FCSTD DOCUMENT  (FreeCAD 0.19R)
Label: card
License: All rights reserved
LicenseURL: http://en.wikipedia.org/wiki/All_rights_reserved
objects: Sketcher::SketchObject×1, PartDesign::Body×1
note: 2 computed .brp shape members not serialized (recipe doc carries the construction recipe); baked Part::Feature solids carry a one-line shape summary decoded from their .brp

FEATURE [Sketcher::SketchObject] Sketch
  FullyConstrained = true
  MapMode = 5
  Support = -> [XY_Plane]
  sketch-geometry (15):
    g0: LineSegment StartX=-48 StartY=35.5 StartZ=0 EndX=48 EndY=35.5 EndZ=0
    g1: LineSegment StartX=50 StartY=33.5 StartZ=0 EndX=50 EndY=-33.5 EndZ=0
    g2: LineSegment StartX=48 StartY=-35.5 StartZ=0 EndX=-48 EndY=-35.5 EndZ=0
    g3: LineSegment StartX=-50 StartY=-33.5 StartZ=0 EndX=-50 EndY=33.5 EndZ=0
    g4: LineSegment StartX=-50 StartY=35.5 StartZ=0 EndX=50 EndY=-35.5 EndZ=0
    g5: LineSegment StartX=50 StartY=35.5 StartZ=0 EndX=-50 EndY=-35.5 EndZ=0
    g6: GeomPoint X=0 Y=0 Z=0
    g7: ArcOfCircle CenterX=-48 CenterY=33.5 CenterZ=0 NormalX=0 NormalY=0 NormalZ=1 AngleXU=0 Radius=2 StartAngle=1.5708 EndAngle=3.14159
    g8: GeomPoint X=-50 Y=35.5 Z=0
    g9: ArcOfCircle CenterX=48 CenterY=33.5 CenterZ=0 NormalX=0 NormalY=0 NormalZ=1 AngleXU=0 Radius=2 StartAngle=1e-16 EndAngle=1.5708
    g10: GeomPoint X=50 Y=35.5 Z=0
    g11: ArcOfCircle CenterX=48 CenterY=-33.5 CenterZ=0 NormalX=0 NormalY=0 NormalZ=1 AngleXU=0 Radius=2 StartAngle=4.71239 EndAngle=6.28319
    g12: GeomPoint X=50 Y=-35.5 Z=0
    g13: ArcOfCircle CenterX=-48 CenterY=-33.5 CenterZ=0 NormalX=0 NormalY=0 NormalZ=1 AngleXU=0 Radius=2 StartAngle=3.14159 EndAngle=4.71239
    g14: GeomPoint X=-50 Y=-35.5 Z=0
  constraints (33):
    c: Horizontal(g0)
    c: Horizontal(g2)
    c: Vertical(g1)
    c: Vertical(g3)
    c: Coincident(g4,g8)
    c: Coincident(g4,g12)
    c: Coincident(g5,g10)
    c: Coincident(g5,g14)
    c: PointOnObject(g6,g4)
    c: PointOnObject(g6,g5)
    c: Coincident(g6,g-1)
    c: DistanceX(g8,g10) = 100
    c: DistanceY(g12,g10) = 71
    c: PointOnObject(g8,g0)
    c: PointOnObject(g8,g3)
    c: Tangent(g0,g7) = 1.5708
    c: Tangent(g3,g7) = 1.5708
    c: Radius(g7) = 2
    c: PointOnObject(g10,g1)
    c: PointOnObject(g10,g0)
    c: Tangent(g1,g9) = 1.5708
    c: Tangent(g0,g9) = 1.5708
    c: Radius(g9) = 2
    c: PointOnObject(g12,g1)
    c: PointOnObject(g12,g2)
    c: Tangent(g1,g11) = 1.5708
    c: Tangent(g2,g11) = 1.5708
    c: Radius(g11) = 2
    c: PointOnObject(g14,g2)
    c: PointOnObject(g14,g3)
    c: Tangent(g2,g13) = 1.5708
    c: Tangent(g3,g13) = 1.5708
    c: Radius(g13) = 2
FEATURE [PartDesign::Body] Body
  Group = -> [Sketch]
  Origin = -> Origin
